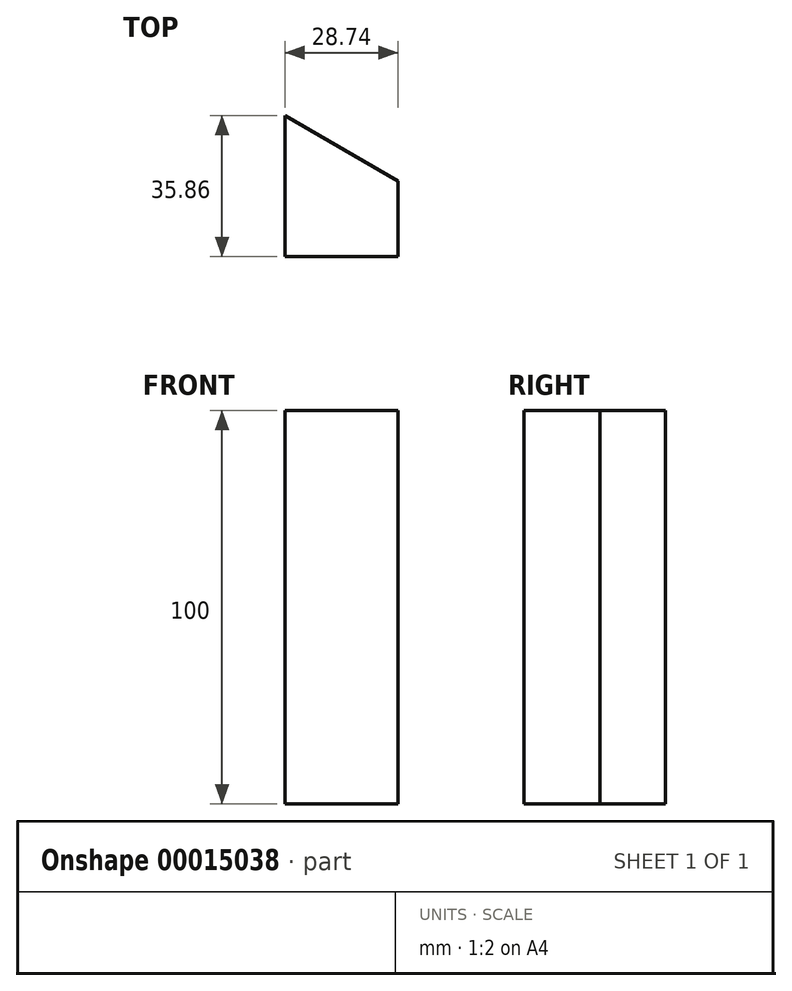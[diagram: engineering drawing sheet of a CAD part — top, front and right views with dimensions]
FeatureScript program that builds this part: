
annotation { "Feature Type Name" : "Feature", "Feature Type Description" : "" }
export const myFeature = defineFeature(function(context is Context, id is Id, definition is map)
    precondition{}
    {
        {
            var Q0;
            Q0=qCreatedBy(makeId("Top.planeOp"),FACE);
            var sketch = newSketch(context, id + "F0", { "sketchPlane" : qUnion([Q0])});
            skLineSegment(sketch, "E0", {"start": v(0, 0) * mm, "end": v(28.74, 0) * mm});
            skLineSegment(sketch, "E1", {"start": v(28.74, 0) * mm, "end": v(28.74, 19.3) * mm});
            skLineSegment(sketch, "E2", {"start": v(28.74, 19.3) * mm, "end": v(0, 35.86) * mm});
            skLineSegment(sketch, "E3", {"start": v(0, 35.86) * mm, "end": v(0, 0) * mm});
            skSolve(sketch);
        }
        {
            var Q0;
            Q0=makeQuery(id+"F0.imprint","IMPRINT",FACE,{"disambiguationData":[TD([[makeQuery(id+"F0.imprint","IMPRINT",EDGE,{"derivedFrom":sQuery(id+"F0.wireOp",EDGE,"E0")}),1.0]])]});
            extrude(context, id + "F1", {"entities" : qUnion([Q0]), "depth" : 100 * mm});
        }
    });
